# Revit family: Switch Flush Mounted Intermediate Switch - generic
name_source: partatom
category: Electrical Fixtures
units: mm (PartAtom-declared; Revit-internal decimal feet)

## family parameters
Always vertical = Yes
Cut with Voids When Loaded = No
Maintain Annotation Orientation = No
OmniClass Number = 23.80.50.00
OmniClass Title = Terminals for Power Supply
Part Type = Normal
Room Calculation Point = No
Round Connector Dimension = Use Diameter
Shared = No
Work Plane-Based = No

## types (1)
- Switch Flush Mounted Intermediate Switch
    Default Elevation = 0 mm  [stored 0 ft]
    Description = Switch Flush Mounted Intermediate Switch
    Manufacturer = Sg Armaturen
    Model = Switch Flush Mounted Intermediate Switch
    URL = https://www.sg-as.com

note: [stored X ft] marks values corroborated as IEEE doubles in the binary element streams (Revit-internal decimal feet)

## geometry (parser evidence)
native form markers: Sweep x21
no freeform markers — native parametric forms only
